# Revit family: 0047102
name_source: partatom
category: Lighting Fixtures
revit_build: Autodesk Revit 2017 (Build: 20190507_1515(x64)
units: mm (PartAtom-declared; Revit-internal decimal feet)

## family parameters
Always vertical = Yes
Cut with Voids When Loaded = No
Light Source = Yes
OmniClass Number = 23.80.70.00
OmniClass Title = Lighting
Part Type = Normal
Room Calculation Point = No
Round Connector Dimension = Use Diameter
Shared = No
Work Plane-Based = No

## types (2) — shared parameters
0_18W_SYL = Yes
Apparent Load = 18 VA
Assembly Code = D5020200
AssetType = Fixed
BACK_PL_EXTR_END(-1)_SYL = 3 mm  [stored 0.00984252 ft]
BACK_PL_EXTR_END_SYL = -3 mm  [stored -0.00984252 ft]
BACK_PL_EXTR_ST(-1)_SYL = 6 mm  [stored 0.019685 ft]
BACK_PL_EXTR_ST_SYL = -6 mm  [stored -0.019685 ft]
BACK_RAIL_SIDE_DIST_SYL = 18 mm  [stored 0.0590551 ft]
BACK_RAIL_WIDTH_SYL = 1 mm  [stored 0.00328084 ft]
BOX_BOTT_DIST_SYL = 28 mm  [stored 0.0918635 ft]
BOX_DEPTH_SYL = 14 mm  [stored 0.0459318 ft]
BOX_TOP_DIST_SYL = 11 mm  [stored 0.0360892 ft]
BOX_WIDTH_SYL = 46 mm  [stored 0.150919 ft]
BRACKET_HOLDER_DEPTH_SYL = 6 mm  [stored 0.019685 ft]
BRACKET_HOLDER_DIST_BOTT_SYL = 22 mm  [stored 0.0721785 ft]
BRACKET_HOLDER_DIST_SIDE_SYL = 3 mm  [stored 0.00984252 ft]
BRACKET_HOLDER_HEIGHT_SYL = 17 mm
BRACKET_HOLDER_WIDTH_SYL = 12 mm  [stored 0.0393701 ft]
B_RAIL_CHAMFER_SYL = 7 mm  [stored 0.0229659 ft]
B_RAIL_DEPTH_SYL = 44 mm
B_RAIL_HEIGHT_SYL = 27 mm
B_RAIL_R_DIST_SYL = 7 mm  [stored 0.0229659 ft]
CABLES_DIST_SYL = 56 mm  [stored 0.183727 ft]
CABLE_FRONT_DIST_SYL = 18 mm  [stored 0.0590551 ft]
CABLE_LENGTH_SYL = 5 mm  [stored 0.0164042 ft]
CABLE_SIDE_DIST_SYL = 29 mm  [stored 0.0951444 ft]
ClassificationName = Uniclass2015
ClassificationValue = EF_70_80
Color Filter = 16777215
DIF_HEIGHT_SYL = 36 mm  [stored 0.11811 ft]
DIF_WIDTH_SYL = 49 mm  [stored 0.160761 ft]
Dimming Lamp Color Temperature Shift = <None>
DocumentationLiterature = http://www.sylvania-lighting.com
ElectricShockClassification = Class I
IfcExportAs = IfcLightFixtureType
IfcExportType = IfcLightFixtureType
ImpactProtectionIndex = IK06
IngressProtection = IP65
Keynote = 16500
LUM_DEPTH_SYL = 28 mm  [stored 0.0918635 ft]
LUM_EXTR_ST_SYL = -5 mm  [stored -0.0164042 ft]
LUM_HEIGHT_SYL = 43 mm  [stored 0.141076 ft]
LUM_WIDTH_SYL = 57 mm  [stored 0.187008 ft]
Lamp = LED
LampColourRenderingIndex = 80
LampMacAdamStep = 5
LampsType = LED
Manufacturer = Feilo Sylvania
ManufacturerName = Feilo Sylvania
Material_1_FEILO = <By Category>
Material_2_FEILO = Default New Material
Material_3_FEILO = <By Category>
Material_4_FEILO = <By Category>
NominalHeight = 26 mm
NominalLength = 110 mm
PowerConsumption = 18 W
PowerFactor = 0.9
Tilt Angle = 0.00°
URL = http://www.sylvania-lighting.com
Voltage = 0 V
Weight = 2.34 kg
zero-valued in all types: LUM_EXTR_END_SYL, NominalWidth

## per-type parameters (varying)
| type | LampColourTemperature | LampNominalLuminous | LuminousEfficacy | Model | ModelNumber | ModelReference | Name | Photometric Web File | TypeName |
| 0047103 SYLFLOOD IP65 2000LM 840 BLACK | 4000 K | 2000 lm | 111 lm/W | SylFlood IP65 2000LM 840 Black | 0047103 | SylFlood IP65 2000LM 840 Black | SylFlood IP65 2000LM 840 Black | 0047103.ies | SylFlood IP65 2000LM 840 Black |
| 0047102 SYLFLOOD IP65 1850LM 830 BLACK | 3000 K | 1850 lm | 103 lm/W | SylFlood IP65 1850LM 830 Black | 0047102 | SylFlood IP65 1850LM 830 Black | SylFlood IP65 1850LM 830 Black | 0047102.ies | SylFlood IP65 1850LM 830 Black |

note: [stored X ft] marks values corroborated as IEEE doubles in the binary element streams (Revit-internal decimal feet)

## geometry (parser evidence)
native form markers: Sweep x9
no freeform markers — native parametric forms only
